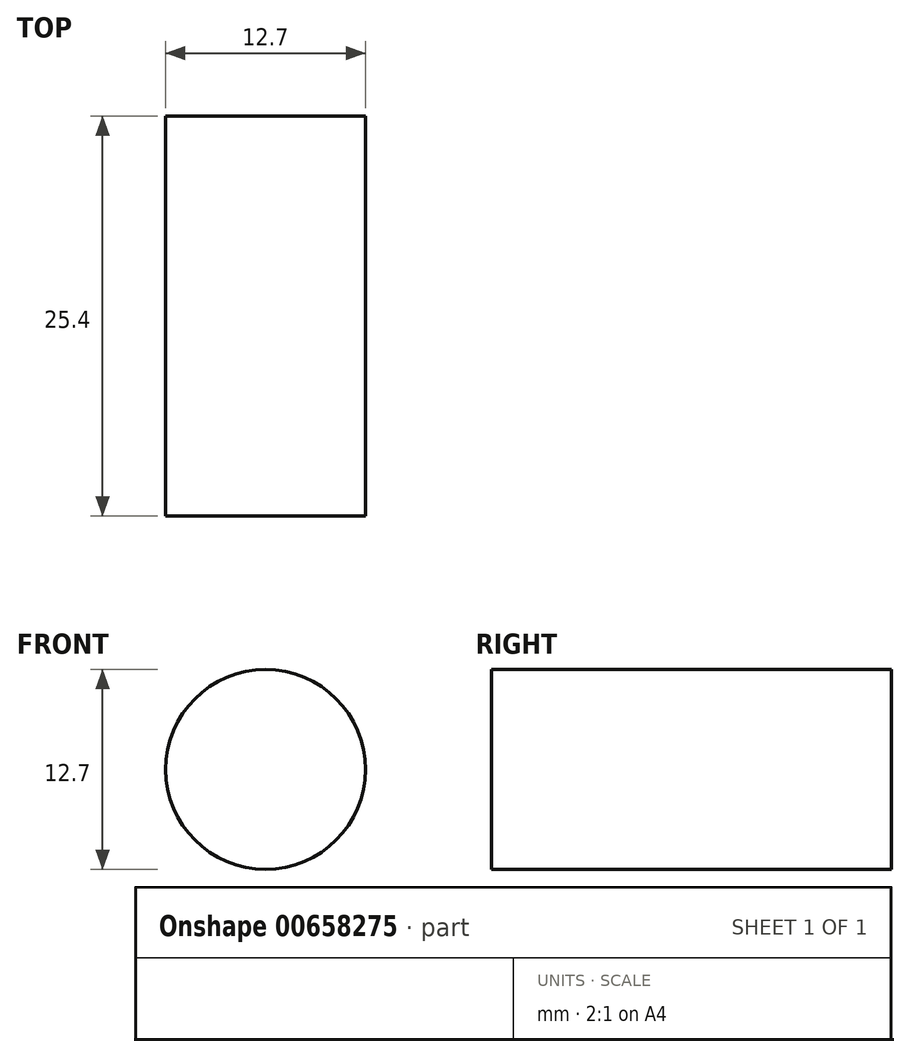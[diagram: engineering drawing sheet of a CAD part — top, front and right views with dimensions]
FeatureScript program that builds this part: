
annotation { "Feature Type Name" : "Feature", "Feature Type Description" : "" }
export const myFeature = defineFeature(function(context is Context, id is Id, definition is map)
    precondition{}
    {
        {
            var Q0;
            Q0=qCreatedBy(makeId("Front.planeOp"),FACE);
            var sketch = newSketch(context, id + "F0", { "sketchPlane" : qUnion([Q0])});
            skCircle(sketch, "E0", {"center": v(0, 0) * mm, "radius": 6.35 * mm});
            skSolve(sketch);
        }
        {
            var Q0;
            Q0=makeQuery(id+"F0.imprint","IMPRINT",FACE,{"disambiguationData":[TD([[makeQuery(id+"F0.imprint","IMPRINT",EDGE,{"derivedFrom":sQuery(id+"F0.wireOp",EDGE,"E0")}),1.0]])]});
            extrude(context, id + "F1", {"entities" : qUnion([Q0]), "depth" : 25.4 * mm, "offsetDistance" : 25.4 * mm});
        }
    });
